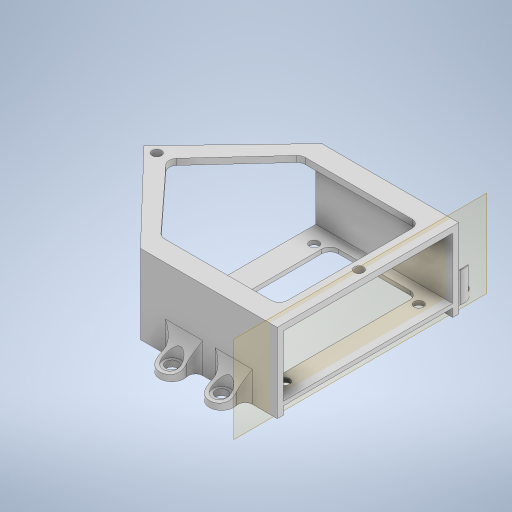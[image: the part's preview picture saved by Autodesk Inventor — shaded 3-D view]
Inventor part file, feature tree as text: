
AUTODESK INVENTOR PART (.ipt)
format: ipt  version: 2023 (Build 270158000, 158)  size: 486,912 bytes
history: native  units: in
note: dims shown in document units (in); Inventor stores cm internally (conversion verified against a paired STEP export)
features: extrude x8, sketch x7, projected_geometry x2, fillet x1, plane x1
ambient origin geometry x8: Origin, YZ Plane, XZ Plane, XY Plane, X Axis, Y Axis, Z Axis, Center Point
bodies: Solid1 (feature_tree)
feature tree (19):
  sketch  "Sketch1"  dims[d0=3.2874in d1=0.1181in]
  extrude  "Extrusion1"  Depth=0.1181in
  extrude  "Extrusion2"  Depth=0.1969in
  extrude  "Extrusion3"  Depth=0.4724in
  sketch  "Sketch3"  dims[d5=0.1969in d6=0.4724in]
  extrude  "Extrusion5"  Depth=0.4724in
  extrude  "Extrusion6"  Depth=1.6437in
  fillet  "Fillet1"  Radius=0.0787in
  extrude  "Extrusion7"  Depth=0.2756in
  extrude  "Extrusion8"  Depth=0.4724in
  plane  "Work Plane1"
  extrude  "Extrusion9"  Depth=0.4724in
  sketch  "Sketch2"  dims[d2=0.1181in d4=0.1969in]
  projected_geometry  "Projected Loop1"
  projected_geometry  "Projected Loop2"
  sketch  "Sketch4"  dims[d7=0.4724in d8=2.6575in]
  sketch  "Sketch6"  dims[d9=1.3287in d10=1.6437in d11=0.0787in d12=0.0in]
  sketch  "Sketch7"  dims[d13=1.2598in d14=0.1575in d15=0.0in d16=0.0in d18=0.2756in]
  sketch  "Sketch8"  dims[d19=0.2756in d20=4.3504in d21=3.563in d22=0.1181in d23=0.0in d24=0.3543in d27=0.185in d33=0.1181in d34=0.0in d35=0.185in d36=0.313in d37=0.3445in d38=0.313in d39=0.3445in d40=0.1181in d41=0.0in d42=0.3543in d43=3.9252in d44=0.1772in d45=0.1575in d46=0.2362in d47=0.2362in d48=0.2362in d49=0.2362in d51=0.4724in d54=0.1378in d55=0.9646in d56=1.9291in d57=0.4823in d58=0.9646in d59=0.5906in d60=0.0in d61=0.3346in d62=0.3346in d63=0.3346in d64=0.3346in d65=0.4724in d66=0.0in d67=1.1811in d68=0.1181in d69=2.7559in d70=0.0in d71=0.1181in d72=0.3346in d31=0.0197in d32=0.0344in]
